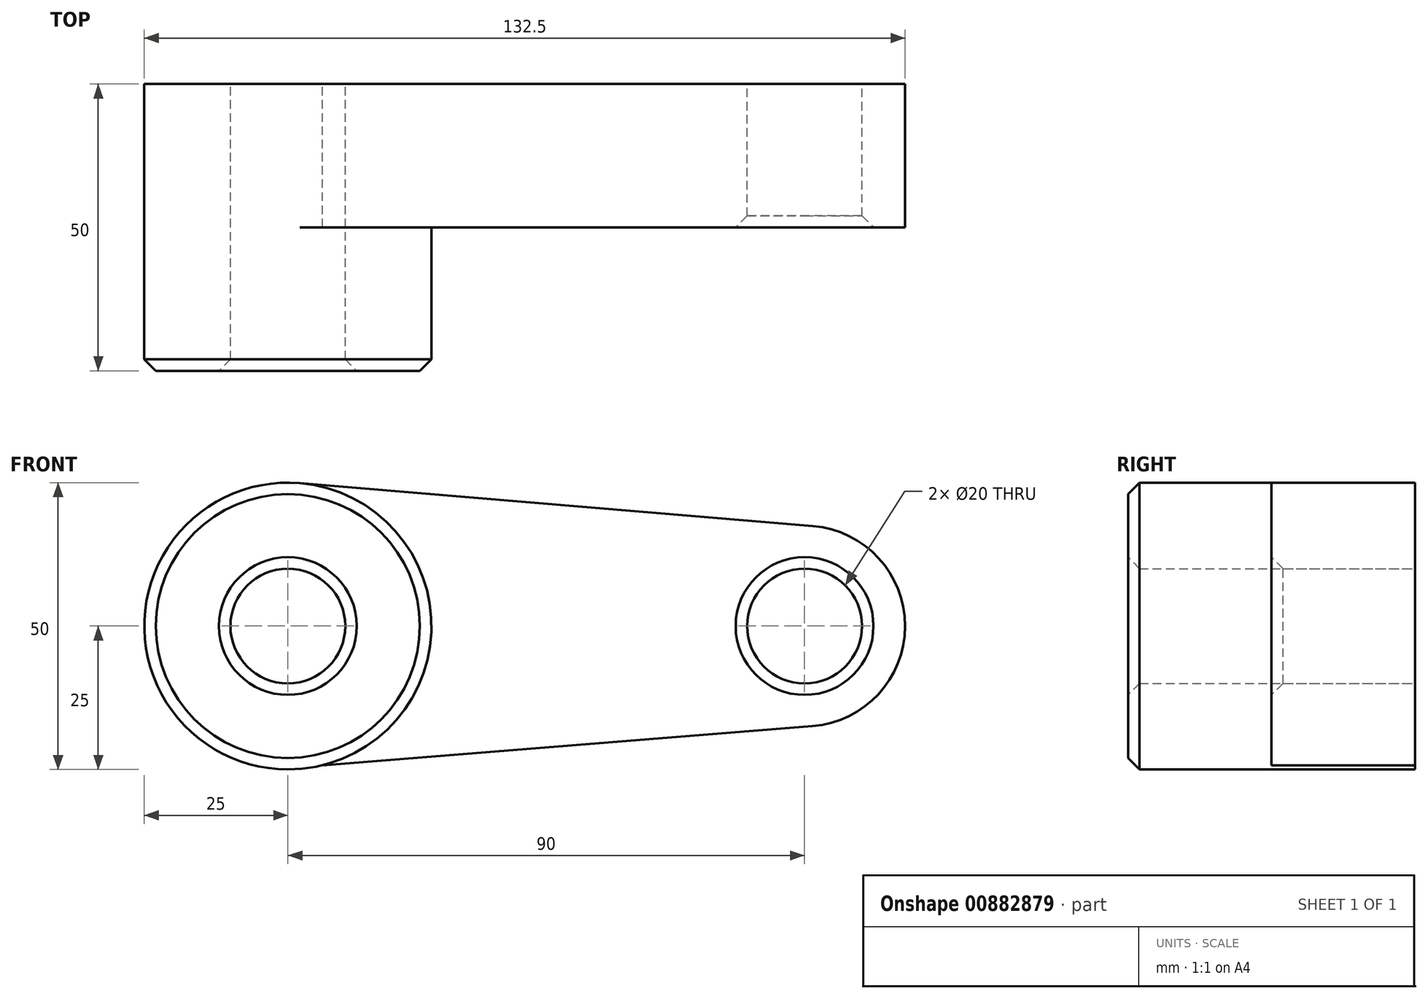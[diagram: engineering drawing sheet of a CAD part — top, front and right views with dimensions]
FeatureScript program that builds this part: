
annotation { "Feature Type Name" : "Feature", "Feature Type Description" : "" }
export const myFeature = defineFeature(function(context is Context, id is Id, definition is map)
    precondition{}
    {
        {
            var Q0;
            Q0=qCreatedBy(makeId("Front.planeOp"),FACE);
            var sketch = newSketch(context, id + "F0", { "sketchPlane" : qUnion([Q0])});
            skCircle(sketch, "E0", {"center": v(0, 0) * mm, "radius": 25 * mm});
            skCircle(sketch, "E1", {"center": v(90, 0) * mm, "radius": 17.5 * mm});
            skLineSegment(sketch, "E2", {"start": v(2.08, 24.91) * mm, "end": v(91.46, 17.44) * mm});
            skLineSegment(sketch, "E3", {"start": v(6, -24.27) * mm, "end": v(91.4, -17.44) * mm});
            skLineSegment(sketch, "E4", {"start": v(91.4, -17.44) * mm, "end": v(40.32, -21.53) * mm});
            skCircle(sketch, "E5", {"center": v(0, 0) * mm, "radius": 10 * mm});
            skCircle(sketch, "E6", {"center": v(90, 0) * mm, "radius": 10 * mm});
            skSolve(sketch);
        }
        {
            var Q0;
            Q0 = qSketchRegion(id + "F0", true);
            extrude(context, id + "F1", {"entities" : qUnion([Q0]), "depth" : 25 * mm, "offsetDistance" : 25 * mm});
        }
        {
            var Q0;
            Q0=makeQuery(id+"F0.imprint","IMPRINT",FACE,{"disambiguationData":[TD([[makeQuery(id+"F0.imprint","IMPRINT",EDGE,{"derivedFrom":sQuery(id+"F0.wireOp",EDGE,"E5")}),-1.0]])]});
            extrude(context, id + "F2", {"entities" : qUnion([Q0]), "operationType" : NewBodyOperationType.ADD, "depth" : 50 * mm, "offsetDistance" : 25 * mm});
        }
        {
            var Q0;
            Q0=makeQuery(id+"F2.opExtrude","CAP_EDGE",EDGE,{"disambiguationData":[OSD([sQuery(id+"F0.wireOp",EDGE,"E0")])],"isStart":false});
            var Q1;
            Q1=makeQuery(id+"F2.opExtrude","CAP_EDGE",EDGE,{"disambiguationData":[OSD([sQuery(id+"F0.wireOp",EDGE,"E5")])],"isStart":false});
            var Q2;
            Q2=makeQuery(id+"F1.opExtrude","CAP_EDGE",EDGE,{"disambiguationData":[OSD([sQuery(id+"F0.wireOp",EDGE,"E6")])],"isStart":false});
            chamfer(context, id + "F3", {"entities" : qUnion([Q0, Q1, Q2]), "width" : 2 * mm, "tangentPropagation" : true});
        }
    });
